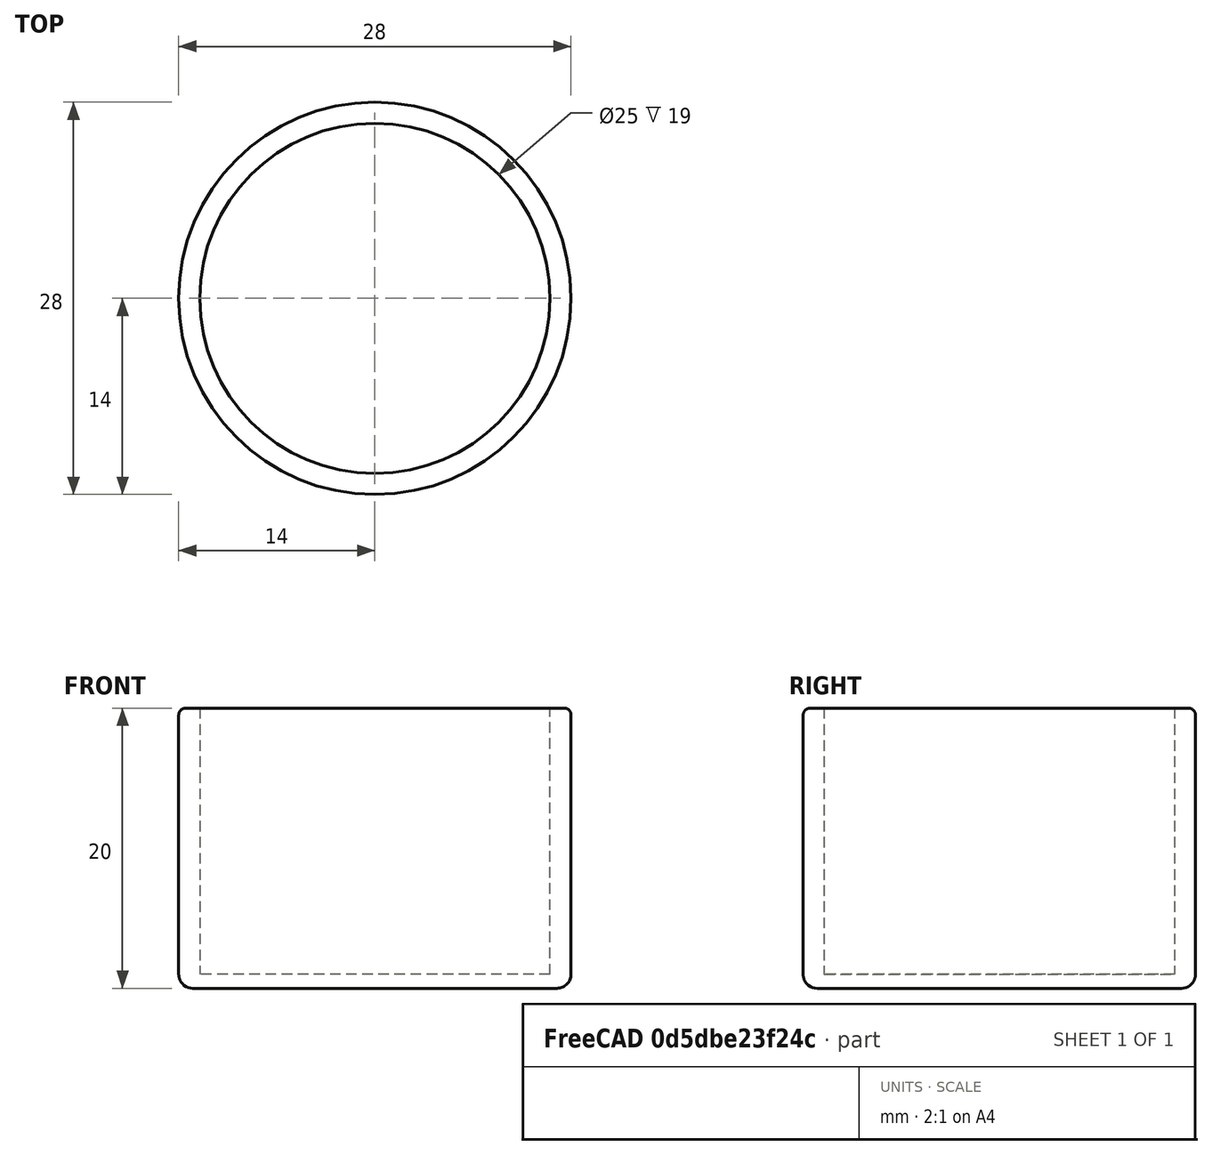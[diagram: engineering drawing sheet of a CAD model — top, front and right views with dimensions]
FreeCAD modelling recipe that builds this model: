
FCSTD DOCUMENT  (FreeCAD 1.0R39109 (Git))
Label: antenna_cap
License: All rights reserved
objects: Sketcher::SketchObject×2, PartDesign::Fillet×2, PartDesign::Pad×1, PartDesign::Pocket×1, PartDesign::Body×1, Mesh::Feature×1
note: 17 computed .brp shape members not serialized (recipe doc carries the construction recipe); baked Part::Feature solids carry a one-line shape summary decoded from their .brp

FEATURE [Sketcher::SketchObject] Sketch
  ArcFitTolerance = 1e-06
  AttachmentSupport = -> [XY_Plane]
  FullyConstrained = true
  MakeInternals = false
  MapMode = 5
  sketch-geometry (1):
    g0: Circle CenterX=0 CenterY=0 CenterZ=0 NormalX=0 NormalY=0 NormalZ=1 AngleXU=0 Radius=14
  constraints (2):
    c: Coincident(g0,g-1)
    c: Diameter(g0) = 28
FEATURE [PartDesign::Pad] Pad
  Direction = (0,0,1)
  Length = 20
  Length2 = 10
  Profile = -> Sketch
  ReferenceAxis = -> Sketch [N_Axis]
  Refine = true
  Suppressed = false
  Type = 0
FEATURE [Sketcher::SketchObject] Sketch001
  ArcFitTolerance = 1e-06
  AttachmentOffset = pos=(0,0,1) rot=(0,0,1;0rad)
  AttachmentSupport = -> [XY_Plane]
  FullyConstrained = true
  MakeInternals = false
  MapMode = 5
  Placement = pos=(0,0,1) rot=(0,0,1;0rad)
  sketch-geometry (1):
    g0: Circle CenterX=0 CenterY=0 CenterZ=0 NormalX=0 NormalY=0 NormalZ=1 AngleXU=0 Radius=12.5
  constraints (2):
    c: Coincident(g0,g-1)
    c: Diameter(g0) = 25
FEATURE [PartDesign::Pocket] Pocket
  BaseFeature = -> Pad
  Direction = (0,0,-1)
  Length = 5
  Length2 = 5
  Profile = -> Sketch001
  ReferenceAxis = -> Sketch001 [N_Axis]
  Refine = true
  Reversed = true
  Suppressed = false
  Type = 1
FEATURE [PartDesign::Fillet] Fillet
  Base = -> Pocket [Edge2]
  BaseFeature = -> Pocket
  Radius = 1
  Refine = true
  SupportTransform = false
  Suppressed = false
  UseAllEdges = false
FEATURE [PartDesign::Fillet] Fillet001
  Base = -> Fillet [Edge3]
  BaseFeature = -> Fillet
  Radius = 0.5
  Refine = true
  SupportTransform = false
  Suppressed = false
  UseAllEdges = false
FEATURE [PartDesign::Body] Body  label="Körper"
  AllowCompound = false
  Group = -> [Sketch,Pad,Sketch001,Pocket,Fillet,Fillet001]
  Origin = -> Origin
  Tip = -> Fillet001
FEATURE [Mesh::Feature] Mesh  label="Fillet001 (Meshed)"
